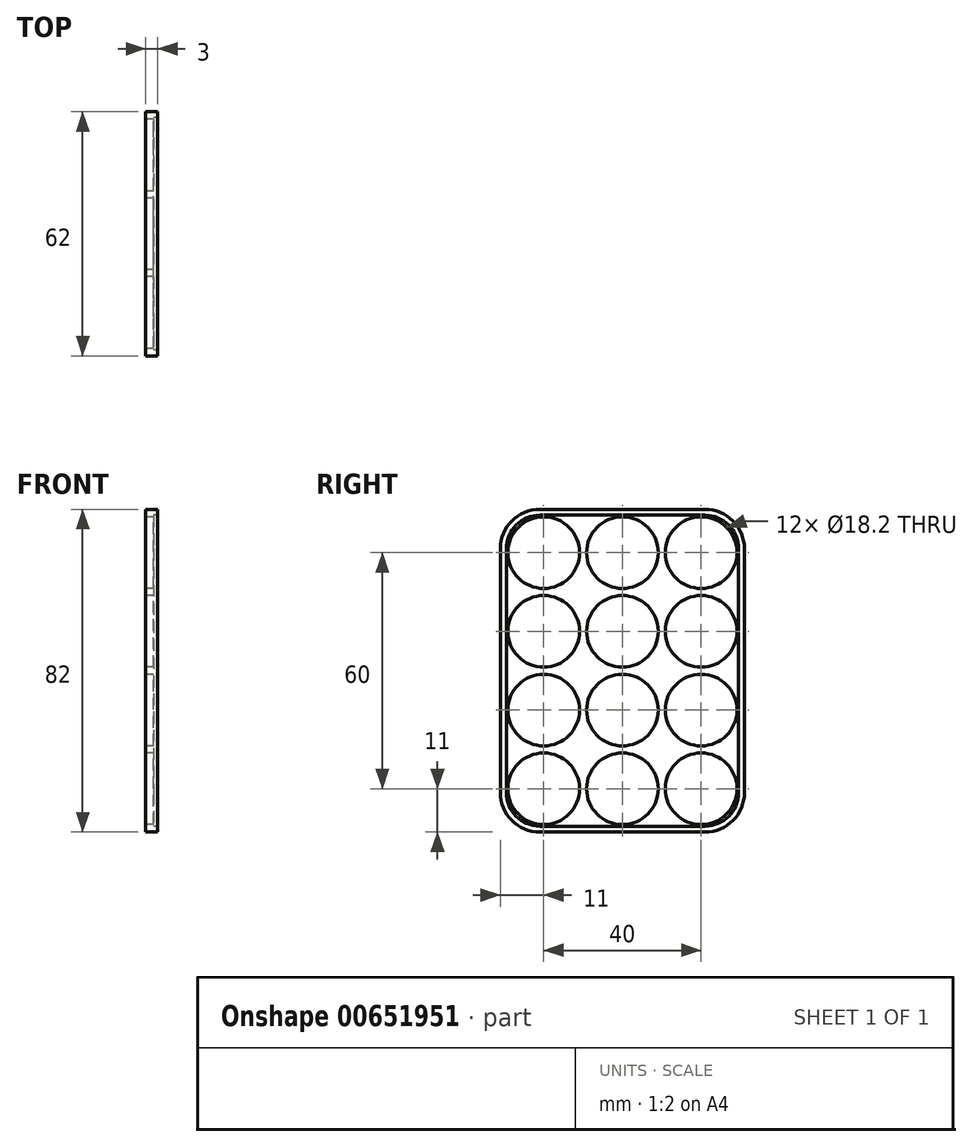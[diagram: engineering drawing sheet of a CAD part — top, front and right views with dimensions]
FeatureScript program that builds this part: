
annotation { "Feature Type Name" : "Feature", "Feature Type Description" : "" }
export const myFeature = defineFeature(function(context is Context, id is Id, definition is map)
    precondition{}
    {
        {
            var Q0;
            Q0=qCreatedBy(makeId("Right.planeOp"),FACE);
            var sketch = newSketch(context, id + "F0", { "sketchPlane" : qUnion([Q0])});
            skLineSegment(sketch, "E0", {"start": v(-42.77, 20) * mm, "end": v(55.8, 20) * mm, "construction": true});
            skLineSegment(sketch, "E1", {"start": v(-46.56, -20) * mm, "end": v(58.65, -20) * mm, "construction": true});
            skLineSegment(sketch, "E2", {"start": v(-48.46, 0) * mm, "end": v(58.65, 0) * mm, "construction": true});
            skLineSegment(sketch, "E3", {"start": v(-48.46, -40) * mm, "end": v(58.65, -40) * mm, "construction": true});
            skLineSegment(sketch, "E4", {"start": v(20, 7.05) * mm, "end": v(20, -12.59) * mm, "construction": true});
            skLineSegment(sketch, "E5", {"start": v(-20, 7.82) * mm, "end": v(-20, -13.1) * mm, "construction": true});
            skCircle(sketch, "E6", {"center": v(-20, -40) * mm, "radius": 9.1 * mm});
            skCircle(sketch, "E7", {"center": v(0, -40) * mm, "radius": 9.1 * mm});
            skCircle(sketch, "E8", {"center": v(20, -40) * mm, "radius": 9.1 * mm});
            skCircle(sketch, "E9", {"center": v(-20, -20) * mm, "radius": 9.1 * mm});
            skCircle(sketch, "E10", {"center": v(0, -20) * mm, "radius": 9.1 * mm});
            skCircle(sketch, "E11", {"center": v(20, -20) * mm, "radius": 9.1 * mm});
            skCircle(sketch, "E12", {"center": v(-20, 0) * mm, "radius": 9.1 * mm});
            skCircle(sketch, "E13", {"center": v(20, 0) * mm, "radius": 9.1 * mm});
            skCircle(sketch, "E14", {"center": v(0, 0) * mm, "radius": 9.1 * mm});
            skCircle(sketch, "E15", {"center": v(-20, 20) * mm, "radius": 9.1 * mm});
            skCircle(sketch, "E16", {"center": v(0, 20) * mm, "radius": 9.1 * mm});
            skCircle(sketch, "E17", {"center": v(20, 20) * mm, "radius": 9.1 * mm});
            skLineSegment(sketch, "E18.bottom", {"start": v(-31, 31) * mm, "end": v(31, 31) * mm});
            skLineSegment(sketch, "E18.top", {"start": v(-31, -51) * mm, "end": v(31, -51) * mm});
            skLineSegment(sketch, "E18.left", {"start": v(-31, 31) * mm, "end": v(-31, -51) * mm});
            skLineSegment(sketch, "E18.right", {"start": v(31, 31) * mm, "end": v(31, -51) * mm});
            skLineSegment(sketch, "E19", {"start": v(-7.47, -10) * mm, "end": v(7.46, -10) * mm, "construction": true});
            skLineSegment(sketch, "E20", {"start": v(0, 20) * mm, "end": v(0, -7.12) * mm, "construction": true});
            skSolve(sketch);
        }
        {
            var Q0;
            Q0=makeQuery(id+"F0.imprint","IMPRINT",FACE,{"disambiguationData":[TD([[makeQuery(id+"F0.imprint","IMPRINT",EDGE,{"derivedFrom":sQuery(id+"F0.wireOp",EDGE,"E6")}),-1.0]])]});
            extrude(context, id + "F1", {"entities" : qUnion([Q0]), "depth" : 2 * mm, "offsetDistance" : 25 * mm});
        }
        {
            var Q0;
            Q0=makeQuery(id+"F1.opExtrude","SWEPT_EDGE",EDGE,{"disambiguationData":[OSD([sQuery(id+"F0.wireOp",EDGE,"E18.bottom"),sQuery(id+"F0.wireOp",EDGE,"E18.right")])]});
            fillet(context, id + "F2", {"entities" : qUnion([Q0]), "tangentPropagation" : true, "radius" : 10 * mm, "defaultsChanged" : true, "vertexSettings" : [], "allowEdgeOverflow" : false});
        }
        {
            var Q0;
            Q0=makeQuery(id+"F1.opExtrude","SWEPT_EDGE",EDGE,{"disambiguationData":[OSD([sQuery(id+"F0.wireOp",EDGE,"E18.bottom"),sQuery(id+"F0.wireOp",EDGE,"E18.left")])]});
            fillet(context, id + "F3", {"entities" : qUnion([Q0]), "tangentPropagation" : true, "radius" : 10 * mm, "defaultsChanged" : true, "vertexSettings" : [], "allowEdgeOverflow" : false});
        }
        {
            var Q0;
            Q0=makeQuery(id+"F1.opExtrude","SWEPT_EDGE",EDGE,{"disambiguationData":[OSD([sQuery(id+"F0.wireOp",EDGE,"E18.top"),sQuery(id+"F0.wireOp",EDGE,"E18.right")])]});
            fillet(context, id + "F4", {"entities" : qUnion([Q0]), "tangentPropagation" : true, "radius" : 10 * mm, "defaultsChanged" : true, "vertexSettings" : [], "allowEdgeOverflow" : false});
        }
        {
            var Q0;
            Q0=makeQuery(id+"F1.opExtrude","SWEPT_EDGE",EDGE,{"disambiguationData":[OSD([sQuery(id+"F0.wireOp",EDGE,"E18.top"),sQuery(id+"F0.wireOp",EDGE,"E18.left")])]});
            fillet(context, id + "F5", {"entities" : qUnion([Q0]), "tangentPropagation" : true, "radius" : 10 * mm, "defaultsChanged" : true, "vertexSettings" : [], "allowEdgeOverflow" : false});
        }
        {
            var Q0;
            Q0=makeQuery(id+"F1.opExtrude","CAP_FACE",FACE,{"disambiguationData":[OSD([sQuery(id+"F0.wireOp",EDGE,"E6"),sQuery(id+"F0.wireOp",EDGE,"E7"),sQuery(id+"F0.wireOp",EDGE,"E8"),sQuery(id+"F0.wireOp",EDGE,"E9"),sQuery(id+"F0.wireOp",EDGE,"E10"),sQuery(id+"F0.wireOp",EDGE,"E11"),sQuery(id+"F0.wireOp",EDGE,"E12"),sQuery(id+"F0.wireOp",EDGE,"E13"),sQuery(id+"F0.wireOp",EDGE,"E14"),sQuery(id+"F0.wireOp",EDGE,"E15"),sQuery(id+"F0.wireOp",EDGE,"E16"),sQuery(id+"F0.wireOp",EDGE,"E17"),sQuery(id+"F0.wireOp",EDGE,"E18.bottom"),sQuery(id+"F0.wireOp",EDGE,"E18.top"),sQuery(id+"F0.wireOp",EDGE,"E18.left"),sQuery(id+"F0.wireOp",EDGE,"E18.right")])],"isStart":false});
            var sketch = newSketch(context, id + "F6", { "sketchPlane" : qUnion([Q0])});
            skLineSegment(sketch, "E21.0", {"start": v(-21, 29.5) * mm, "end": v(21, 29.5) * mm});
            skArc(sketch, "E21.1", {"start": v(29.5, 21) * mm, "mid": v(27.01, 27.01) * mm, "end": v(21, 29.5) * mm});
            skArc(sketch, "E21.2", {"start": v(-21, 29.5) * mm, "mid": v(-27.01, 27.01) * mm, "end": v(-29.5, 21) * mm});
            skLineSegment(sketch, "E21.3", {"start": v(29.5, 21) * mm, "end": v(29.5, -41) * mm});
            skLineSegment(sketch, "E21.4", {"start": v(-29.5, 21) * mm, "end": v(-29.5, -41) * mm});
            skArc(sketch, "E21.5", {"start": v(-29.5, -41) * mm, "mid": v(-27.01, -47.01) * mm, "end": v(-21, -49.5) * mm});
            skLineSegment(sketch, "E21.6", {"start": v(-21, -49.5) * mm, "end": v(21, -49.5) * mm});
            skArc(sketch, "E21.7", {"start": v(21, -49.5) * mm, "mid": v(27.01, -47.01) * mm, "end": v(29.5, -41) * mm});
            skSolve(sketch);
        }
        {
            var Q0;
            Q0=makeQuery(id+"F6.imprint","IMPRINT",FACE,{"disambiguationData":[TD([[makeQuery(id+"F6.imprint","IMPRINT",EDGE,{"derivedFrom":sQuery(id+"F6.wireOp",EDGE,"E21.0")}),1.0]])]});
            extrude(context, id + "F7", {"entities" : qUnion([Q0]), "operationType" : NewBodyOperationType.ADD, "depth" : 1 * mm, "offsetDistance" : 25 * mm});
        }
    });
